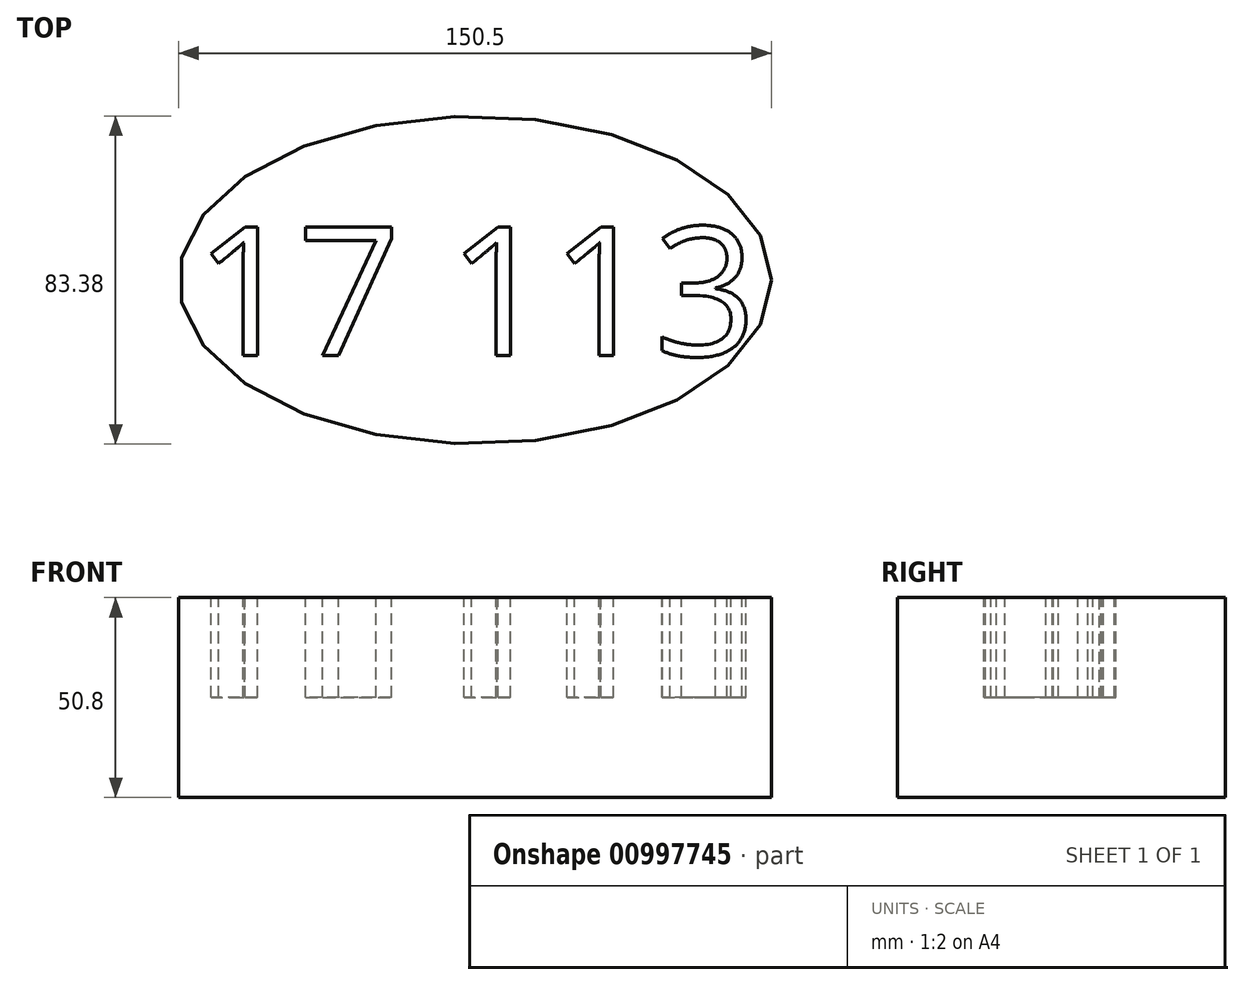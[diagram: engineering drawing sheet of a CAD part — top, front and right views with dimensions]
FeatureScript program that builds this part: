
annotation { "Feature Type Name" : "Feature", "Feature Type Description" : "" }
export const myFeature = defineFeature(function(context is Context, id is Id, definition is map)
    precondition{}
    {
        {
            var Q0;
            Q0=qCreatedBy(makeId("Top.planeOp"),FACE);
            var sketch = newSketch(context, id + "F0", { "sketchPlane" : qUnion([Q0])});
            skEllipse(sketch, "E0", {"center": v(0, 0) * mm, "majorRadius": 75.25 * mm, "minorRadius": 41.69 * mm, "majorAxis": v(1, 0)});
            skSolve(sketch);
        }
        {
            var Q0;
            Q0 = qSketchRegion(id + "F0", true);
            extrude(context, id + "F1", {"entities" : qUnion([Q0]), "depth" : 25.4 * mm, "offsetDistance" : 25.4 * mm});
        }
        {
            var Q0;
            Q0=makeQuery(id+"F1.opExtrude","CAP_FACE",FACE,{"disambiguationData":[OSD([sQuery(id+"F0.wireOp",EDGE,"E0")])],"isStart":false});
            extrude(context, id + "F2", {"entities" : qUnion([Q0]), "operationType" : NewBodyOperationType.ADD, "oppositeDirection" : true, "depth" : 25.4 * mm, "offsetDistance" : 25.4 * mm});
        }
        {
            var Q0;
            Q0=makeQuery(id+"F1.opExtrude","CAP_FACE",FACE,{"disambiguationData":[OSD([sQuery(id+"F0.wireOp",EDGE,"E0")])],"isStart":false});
            extrude(context, id + "F3", {"entities" : qUnion([Q0]), "operationType" : NewBodyOperationType.ADD, "depth" : 25.4 * mm, "offsetDistance" : 25.4 * mm});
        }
        {
            var Q0;
            Q0=makeQuery(id+"F3.opExtrude","CAP_FACE",FACE,{"disambiguationData":[OSD([sQuery(id+"F0.wireOp",EDGE,"E0")])],"isStart":false});
            var sketch = newSketch(context, id + "F4", { "sketchPlane" : qUnion([Q0])});
            skText(sketch, "E1", { "text": "17 113\n", "fontName": "OpenSans-Regular.ttf"});
            const initialGuessF4  = {"E1": [-0.07128, -0.01923, 1, 0, 0.03297]};
            skSetInitialGuess(sketch, initialGuessF4);
            skSolve(sketch);
        }
        {
            var Q0;
            Q0 = qSketchRegion(id + "F4", true);
            extrude(context, id + "F5", {"entities" : qUnion([Q0]), "operationType" : NewBodyOperationType.REMOVE, "oppositeDirection" : true, "depth" : 25.4 * mm, "offsetDistance" : 25.4 * mm});
        }
    });
